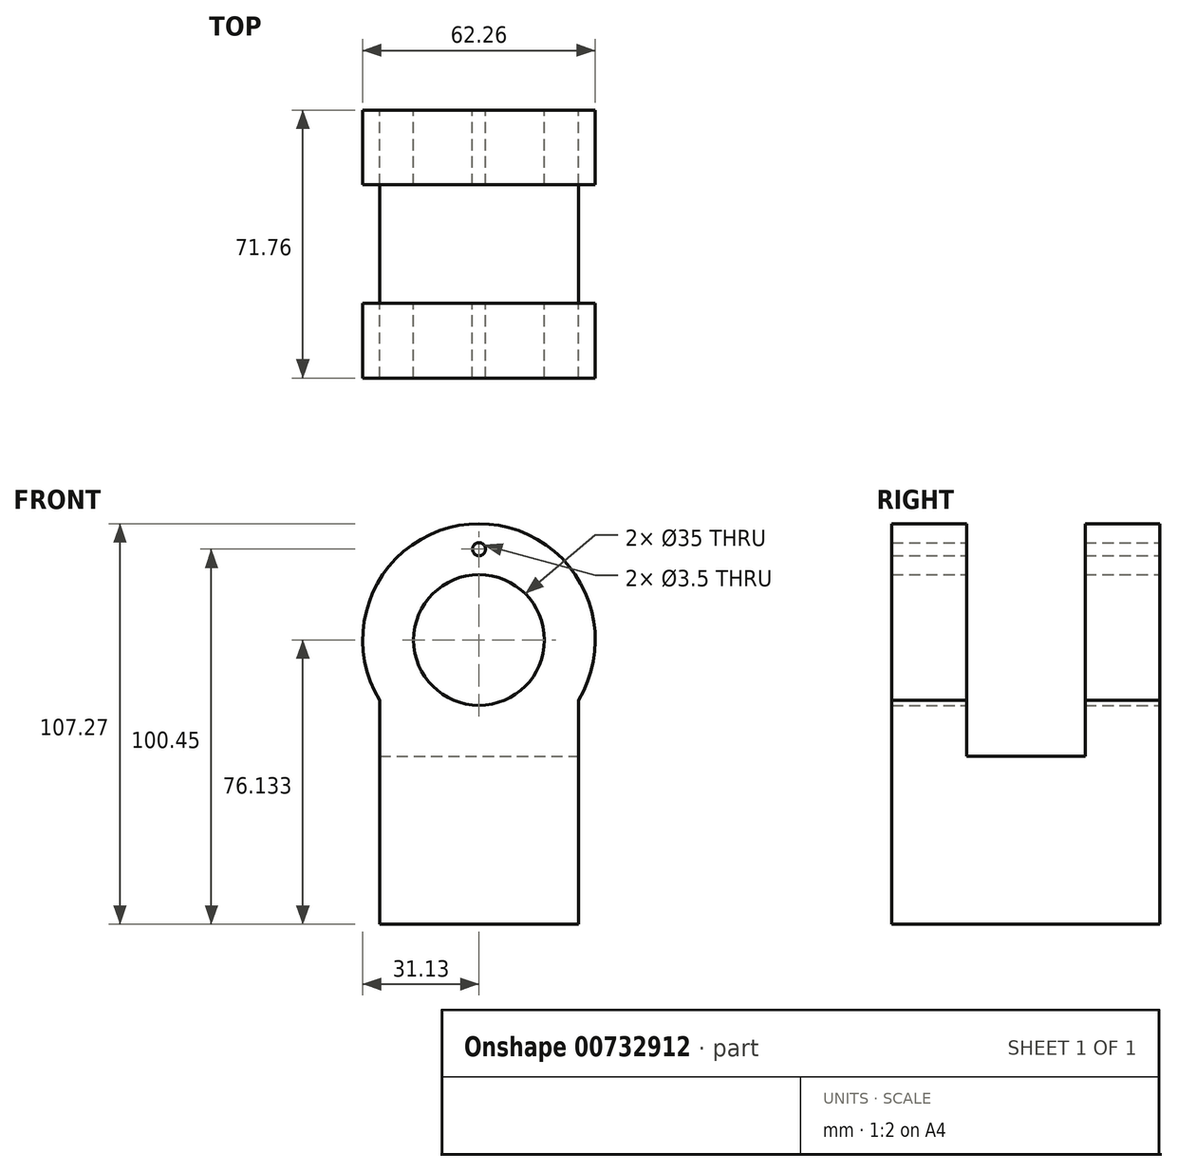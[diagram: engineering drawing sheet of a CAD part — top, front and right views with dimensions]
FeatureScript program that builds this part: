
annotation { "Feature Type Name" : "Feature", "Feature Type Description" : "" }
export const myFeature = defineFeature(function(context is Context, id is Id, definition is map)
    precondition{}
    {
        {
            var Q0;
            Q0=qCreatedBy(makeId("Top.planeOp"),FACE);
            var sketch = newSketch(context, id + "F0", { "sketchPlane" : qUnion([Q0])});
            skLineSegment(sketch, "E0.bottom", {"start": v(-26.63, 15.87) * mm, "end": v(26.63, 15.87) * mm});
            skLineSegment(sketch, "E0.top", {"start": v(-26.63, -15.88) * mm, "end": v(26.63, -15.88) * mm});
            skLineSegment(sketch, "E0.left", {"start": v(-26.63, 15.88) * mm, "end": v(-26.63, -15.87) * mm});
            skLineSegment(sketch, "E0.right", {"start": v(26.63, 15.87) * mm, "end": v(26.63, -15.88) * mm});
            skPoint(sketch, "E0.middle", {"position": v(0, 0) * mm});
            skLineSegment(sketch, "E1.top", {"start": v(-26.63, 35.88) * mm, "end": v(26.63, 35.88) * mm});
            skLineSegment(sketch, "E1.left", {"start": v(-26.63, 15.87) * mm, "end": v(-26.63, 35.88) * mm});
            skLineSegment(sketch, "E1.right", {"start": v(26.63, 15.87) * mm, "end": v(26.63, 35.88) * mm});
            skLineSegment(sketch, "E2.top", {"start": v(-26.63, -35.88) * mm, "end": v(26.63, -35.87) * mm});
            skLineSegment(sketch, "E2.left", {"start": v(-26.63, -15.88) * mm, "end": v(-26.63, -35.88) * mm});
            skLineSegment(sketch, "E2.right", {"start": v(26.63, -15.88) * mm, "end": v(26.63, -35.87) * mm});
            skSolve(sketch);
        }
        {
            var Q0;
            Q0 = qSketchRegion(id + "F0", true);
            extrude(context, id + "F1", {"entities" : qUnion([Q0]), "depth" : 45 * mm, "offsetDistance" : 25 * mm});
        }
        {
            var Q0;
            Q0=makeQuery(id+"F1.opExtrude","CAP_FACE",FACE,{"disambiguationData":[OSD([sQuery(id+"F0.wireOp",EDGE,"E0.left"),sQuery(id+"F0.wireOp",EDGE,"E0.right"),sQuery(id+"F0.wireOp",EDGE,"E1.top"),sQuery(id+"F0.wireOp",EDGE,"E1.left"),sQuery(id+"F0.wireOp",EDGE,"E1.right"),sQuery(id+"F0.wireOp",EDGE,"E2.top"),sQuery(id+"F0.wireOp",EDGE,"E2.left"),sQuery(id+"F0.wireOp",EDGE,"E2.right")])],"isStart":false});
            var sketch = newSketch(context, id + "F2", { "sketchPlane" : qUnion([Q0])});
            skLineSegment(sketch, "E3.bottom", {"start": v(-26.63, 35.88) * mm, "end": v(26.63, 35.88) * mm});
            skLineSegment(sketch, "E3.top", {"start": v(-26.63, 15.88) * mm, "end": v(26.63, 15.88) * mm});
            skLineSegment(sketch, "E3.left", {"start": v(-26.63, 35.88) * mm, "end": v(-26.63, 15.88) * mm});
            skLineSegment(sketch, "E3.right", {"start": v(26.63, 35.88) * mm, "end": v(26.63, 15.88) * mm});
            skLineSegment(sketch, "E4.bottom", {"start": v(-26.63, -35.88) * mm, "end": v(26.63, -35.88) * mm});
            skLineSegment(sketch, "E4.top", {"start": v(-26.63, -15.88) * mm, "end": v(26.63, -15.88) * mm});
            skLineSegment(sketch, "E4.left", {"start": v(-26.63, -35.88) * mm, "end": v(-26.63, -15.88) * mm});
            skLineSegment(sketch, "E4.right", {"start": v(26.63, -35.88) * mm, "end": v(26.63, -15.88) * mm});
            skSolve(sketch);
        }
        {
            var Q0;
            Q0=makeQuery(id+"F2.imprint","IMPRINT",FACE,{"disambiguationData":[TD([[makeQuery(id+"F2.imprint","IMPRINT",EDGE,{"derivedFrom":sQuery(id+"F2.wireOp",EDGE,"E3.bottom")}),-1.0]])]});
            var Q1;
            Q1=makeQuery(id+"F2.imprint","IMPRINT",FACE,{"disambiguationData":[TD([[makeQuery(id+"F2.imprint","IMPRINT",EDGE,{"derivedFrom":sQuery(id+"F2.wireOp",EDGE,"E4.bottom")}),1.0]])]});
            extrude(context, id + "F3", {"entities" : qUnion([Q0, Q1]), "operationType" : NewBodyOperationType.ADD, "depth" : 15 * mm, "offsetDistance" : 25 * mm});
        }
        {
            var Q0;
            Q0=makeQuery(id+"F3.opExtrude","SWEPT_FACE",FACE,{"disambiguationData":[OSD([sQuery(id+"F2.wireOp",EDGE,"E3.top")])]});
            var sketch = newSketch(context, id + "F4", { "sketchPlane" : qUnion([Q0])});
            skCircle(sketch, "E5", {"center": v(0, 76.13) * mm, "radius": 31.13 * mm});
            skPoint(sketch, "E5.first.point", {"position": v(-26.63, 60) * mm});
            skPoint(sketch, "E5.second.point", {"position": v(0, 45) * mm});
            skPoint(sketch, "E5.third.point", {"position": v(26.63, 60) * mm});
            skSolve(sketch);
        }
        {
            var Q0;
            Q0 = qSketchRegion(id + "F4", true);
            extrude(context, id + "F5", {"entities" : qUnion([Q0]), "operationType" : NewBodyOperationType.ADD, "oppositeDirection" : true, "depth" : 20 * mm, "offsetDistance" : 25 * mm});
        }
        {
            var Q0;
            Q0=makeQuery(id+"F3.opExtrude","SWEPT_FACE",FACE,{"disambiguationData":[OSD([sQuery(id+"F2.wireOp",EDGE,"E4.top")])]});
            var sketch = newSketch(context, id + "F6", { "sketchPlane" : qUnion([Q0])});
            skCircle(sketch, "E6", {"center": v(0, 76.13) * mm, "radius": 31.13 * mm});
            skPoint(sketch, "E6.first.point", {"position": v(-26.63, 60) * mm});
            skPoint(sketch, "E6.second.point", {"position": v(0, 45) * mm});
            skPoint(sketch, "E6.third.point", {"position": v(26.63, 60) * mm});
            skSolve(sketch);
        }
        {
            var Q0;
            Q0 = qSketchRegion(id + "F6", true);
            extrude(context, id + "F7", {"entities" : qUnion([Q0]), "operationType" : NewBodyOperationType.ADD, "oppositeDirection" : true, "depth" : 20 * mm, "offsetDistance" : 25 * mm});
        }
        {
            var Q0;
            Q0=makeQuery(id+"F5.boolean.opBoolean","MERGE",FACE,{"derivedFrom":[makeQuery(id+"F3.boolean.opBoolean","MERGE",FACE,{"derivedFrom":[makeQuery(id+"F1.opExtrude","SWEPT_FACE",FACE,{"disambiguationData":[OSD([sQuery(id+"F0.wireOp",EDGE,"E1.top")])]}),makeQuery(id+"F3.opExtrude","SWEPT_FACE",FACE,{"disambiguationData":[OSD([sQuery(id+"F2.wireOp",EDGE,"E3.bottom")])]})]}),makeQuery(id+"F5.opExtrude","CAP_FACE",FACE,{"disambiguationData":[OSD([sQuery(id+"F4.wireOp",EDGE,"E5")])],"isStart":false})]});
            var sketch = newSketch(context, id + "F8", { "sketchPlane" : qUnion([Q0])});
            skCircle(sketch, "E7", {"center": v(0, 76.13) * mm, "radius": 17.5 * mm});
            skSolve(sketch);
        }
        {
            var Q0;
            Q0 = qSketchRegion(id + "F8", true);
            extrude(context, id + "F9", {"entities" : qUnion([Q0]), "operationType" : NewBodyOperationType.REMOVE, "oppositeDirection" : true, "depth" : 100 * mm, "offsetDistance" : 25 * mm});
        }
        {
            var Q0;
            Q0=makeQuery(id+"F5.boolean.opBoolean","MERGE",FACE,{"derivedFrom":[makeQuery(id+"F3.boolean.opBoolean","MERGE",FACE,{"derivedFrom":[makeQuery(id+"F1.opExtrude","SWEPT_FACE",FACE,{"disambiguationData":[OSD([sQuery(id+"F0.wireOp",EDGE,"E1.top")])]}),makeQuery(id+"F3.opExtrude","SWEPT_FACE",FACE,{"disambiguationData":[OSD([sQuery(id+"F2.wireOp",EDGE,"E3.bottom")])]})]}),makeQuery(id+"F5.opExtrude","CAP_FACE",FACE,{"disambiguationData":[OSD([sQuery(id+"F4.wireOp",EDGE,"E5")])],"isStart":false})]});
            var sketch = newSketch(context, id + "F10", { "sketchPlane" : qUnion([Q0])});
            skLineSegment(sketch, "E8", {"start": v(0, 93.63) * mm, "end": v(0, 107.27) * mm});
            skPoint(sketch, "E8.startSnap0", {"position": v(0, 107.27) * mm});
            skCircle(sketch, "E9", {"center": v(0, 100.45) * mm, "radius": 1.75 * mm});
            skSolve(sketch);
        }
        {
            var Q0;
            Q0 = qSketchRegion(id + "F10", true);
            extrude(context, id + "F11", {"entities" : qUnion([Q0]), "operationType" : NewBodyOperationType.REMOVE, "oppositeDirection" : true, "depth" : 100 * mm, "offsetDistance" : 25 * mm});
        }
    });
